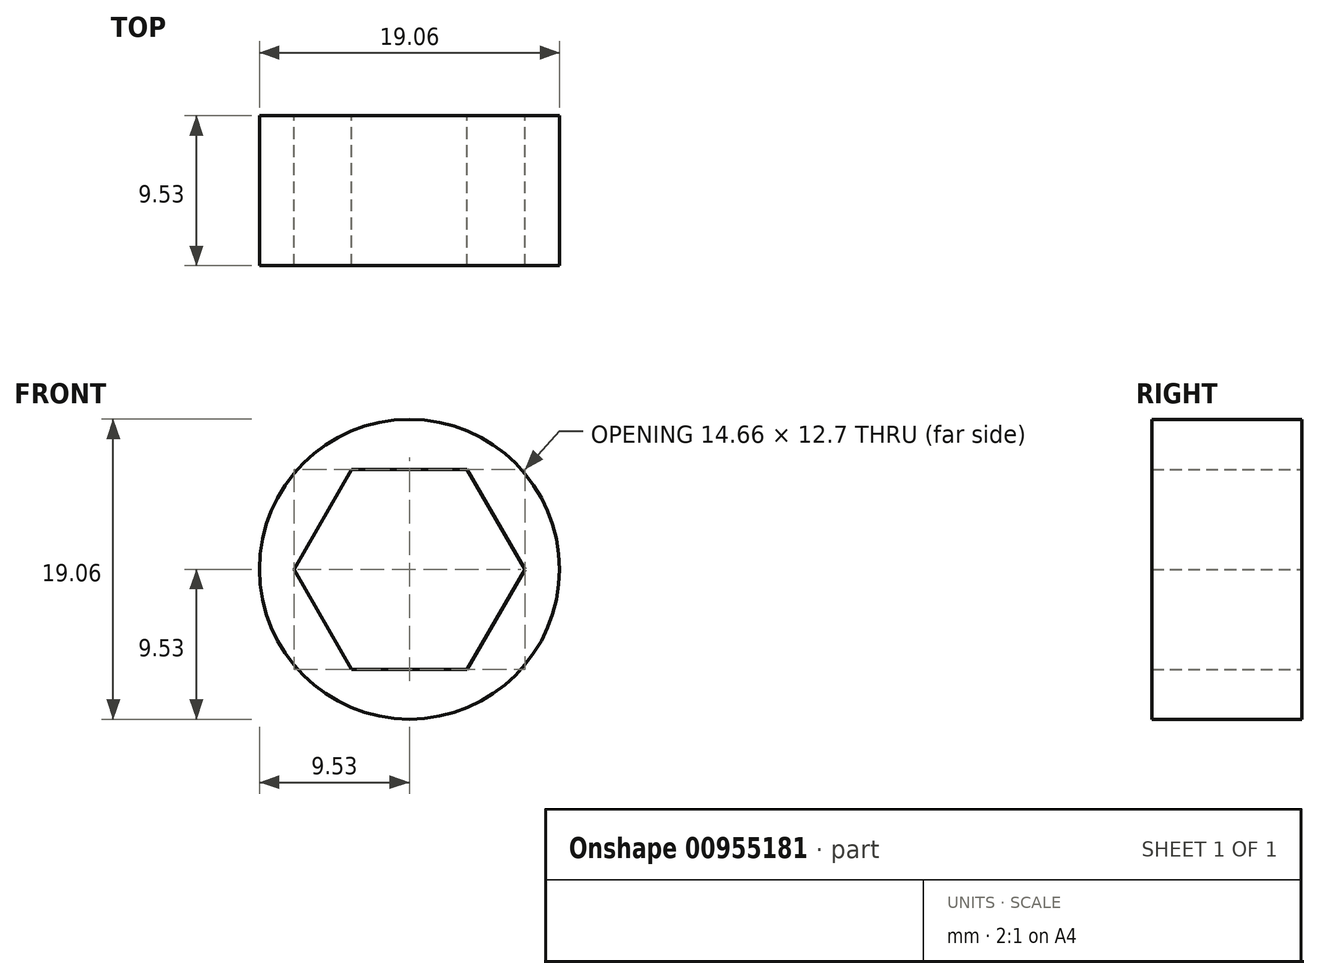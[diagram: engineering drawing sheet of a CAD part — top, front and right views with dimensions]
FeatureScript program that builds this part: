
annotation { "Feature Type Name" : "Feature", "Feature Type Description" : "" }
export const myFeature = defineFeature(function(context is Context, id is Id, definition is map)
    precondition{}
    {
        {
            var Q0;
            Q0=qCreatedBy(makeId("Front.planeOp"),FACE);
            var sketch = newSketch(context, id + "F0", { "sketchPlane" : qUnion([Q0])});
            skCircle(sketch, "E0", {"center": v(0, 0) * mm, "radius": 9.52 * mm});
            skCircle(sketch, "E1.cCircle", {"center": v(0, 0) * mm, "radius": 6.35 * mm, "construction": true});
            skLineSegment(sketch, "E1.0", {"start": v(3.67, -6.35) * mm, "end": v(-3.67, -6.35) * mm});
            skLineSegment(sketch, "E1.1", {"start": v(-3.67, -6.35) * mm, "end": v(-7.33, 0) * mm});
            skLineSegment(sketch, "E1.2", {"start": v(-7.33, 0) * mm, "end": v(-3.67, 6.35) * mm});
            skLineSegment(sketch, "E1.3", {"start": v(-3.67, 6.35) * mm, "end": v(3.67, 6.35) * mm});
            skLineSegment(sketch, "E1.4", {"start": v(3.67, 6.35) * mm, "end": v(7.33, 0) * mm});
            skLineSegment(sketch, "E1.5", {"start": v(7.33, 0) * mm, "end": v(3.67, -6.35) * mm});
            skPoint(sketch, "E1.0.midPoint", {"position": v(0, -6.35) * mm});
            skSolve(sketch);
        }
        {
            var Q0;
            Q0=qSketchRegion(id+"F0",true);
            extrude(context, id + "F1", {"entities" : qUnion([Q0]), "depth" : 9.52 * mm, "offsetDistance" : 25.4 * mm});
        }
    });
